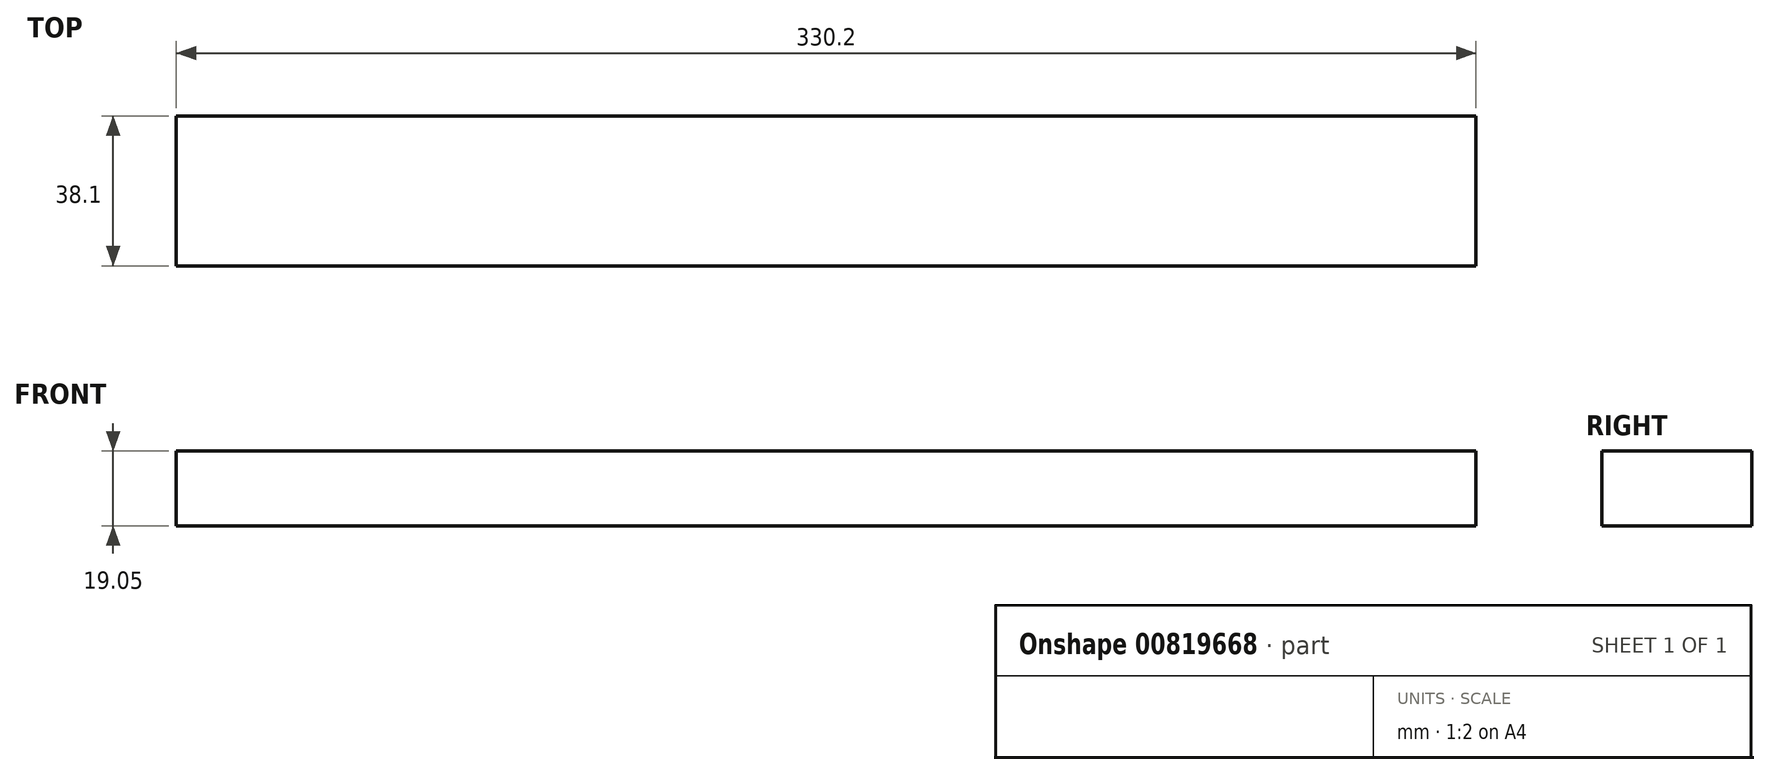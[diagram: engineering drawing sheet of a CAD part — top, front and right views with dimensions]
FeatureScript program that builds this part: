
annotation { "Feature Type Name" : "Feature", "Feature Type Description" : "" }
export const myFeature = defineFeature(function(context is Context, id is Id, definition is map)
    precondition{}
    {
        {
            var Q0;
            Q0=qCreatedBy(makeId("Front.planeOp"),FACE);
            var sketch = newSketch(context, id + "F0", { "sketchPlane" : qUnion([Q0])});
            skLineSegment(sketch, "E0.bottom", {"start": v(262.54, 0) * mm, "end": v(-67.66, 0) * mm});
            skLineSegment(sketch, "E0.top", {"start": v(262.54, 19.05) * mm, "end": v(-67.66, 19.05) * mm});
            skLineSegment(sketch, "E0.left", {"start": v(262.54, 0) * mm, "end": v(262.54, 19.05) * mm});
            skLineSegment(sketch, "E0.right", {"start": v(-67.66, 0) * mm, "end": v(-67.66, 19.05) * mm});
            skSolve(sketch);
        }
        {
            var Q0;
            Q0=qSketchRegion(id+"F0",true);
            extrude(context, id + "F1", {"entities" : qUnion([Q0]), "depth" : 38.1 * mm, "offsetDistance" : 25.4 * mm});
        }
    });
